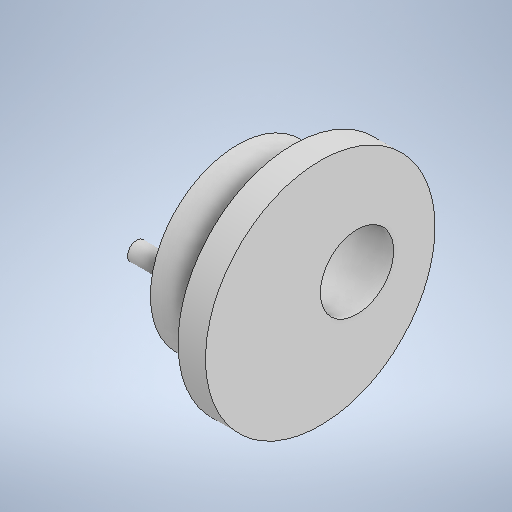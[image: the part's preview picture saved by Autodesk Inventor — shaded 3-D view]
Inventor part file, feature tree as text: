
AUTODESK INVENTOR PART (.ipt)
format: ipt  version: 2025.1 (Build 291241000, 241)  size: 259,072 bytes
history: native  units: mm
features: sketch x3, revolve x1, hole x1, extrude x1
ambient origin geometry x8: Origin, YZ Plane, XZ Plane, XY Plane, X Axis, Y Axis, Z Axis, Center Point
bodies: Solid1 (feature_tree)
feature tree (6):
  revolve  "Revolution1"  [1 undecoded]
  hole  "Hole1"  [1 undecoded]
  extrude  "Extrusion1"  Depth=4.0mm
  sketch  "Sketch1"  dims[d0=3.0mm d1=6.0mm]
  sketch  "Sketch2"  dims[d2=25.0mm d3=19.0mm]
  sketch  "Sketch4"  dims[d4=90.0deg d5=8.0mm d6=6.0mm d7=4.0mm d8=2.0mm d9=90.0deg d10=8.0mm d11=0.0mm d12=4.0mm d21=6.0mm d22=2.0mm d23=5.0mm d24=0.0mm]
note: 2 required parameter values undecoded (feature->parameter linkage not recoverable at this tier; creation-order binding heuristic only, values carry confidence <= 0.55)